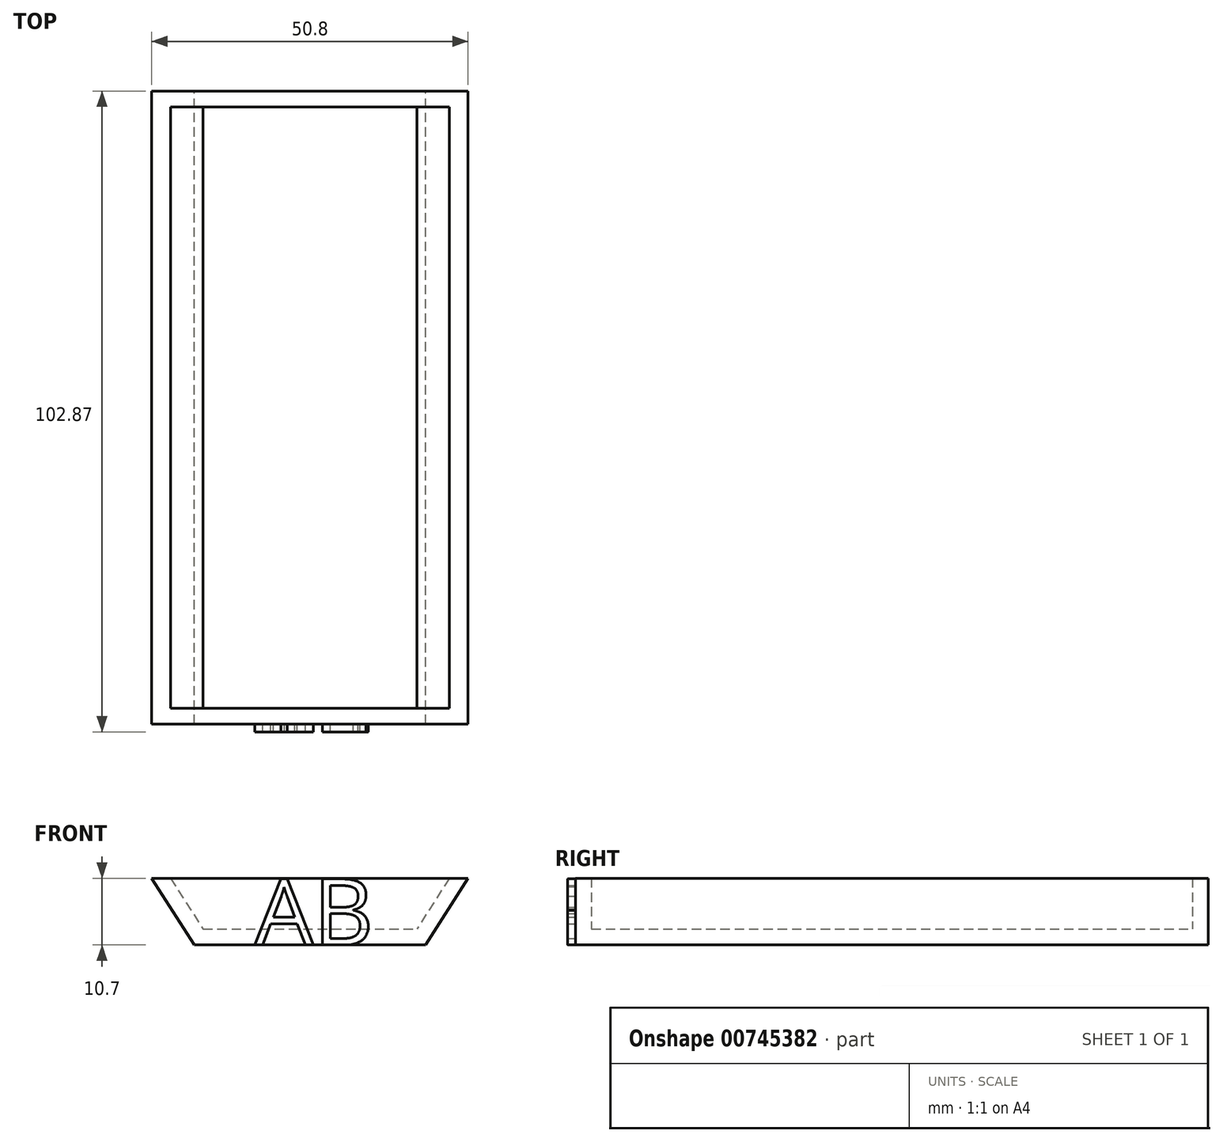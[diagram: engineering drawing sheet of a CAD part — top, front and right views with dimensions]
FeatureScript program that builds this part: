
annotation { "Feature Type Name" : "Feature", "Feature Type Description" : "" }
export const myFeature = defineFeature(function(context is Context, id is Id, definition is map)
    precondition{}
    {
        {
            var Q0;
            Q0=qCreatedBy(makeId("Front.planeOp"),FACE);
            var sketch = newSketch(context, id + "F0", { "sketchPlane" : qUnion([Q0])});
            skLineSegment(sketch, "E0", {"start": v(-50.8, 25.46) * mm, "end": v(0, 25.46) * mm});
            skLineSegment(sketch, "E1", {"start": v(-50.8, 25.46) * mm, "end": v(-43.95, 14.76) * mm});
            skLineSegment(sketch, "E2", {"start": v(0, 25.46) * mm, "end": v(-6.84, 14.76) * mm});
            skLineSegment(sketch, "E3", {"start": v(-43.95, 14.76) * mm, "end": v(-6.84, 14.76) * mm});
            skSolve(sketch);
        }
        {
            var Q0;
            Q0=makeQuery(id+"F0.imprint","IMPRINT",FACE,{"disambiguationData":[TD([[makeQuery(id+"F0.imprint","IMPRINT",EDGE,{"derivedFrom":sQuery(id+"F0.wireOp",EDGE,"E0")}),-1.0]])]});
            extrude(context, id + "F1", {"entities" : qUnion([Q0]), "depth" : 101.6 * mm, "offsetDistance" : 25.4 * mm});
        }
        {
            var Q0;
            Q0=makeQuery(id+"F1.opExtrude","SWEPT_FACE",FACE,{"disambiguationData":[OSD([sQuery(id+"F0.wireOp",EDGE,"E0")])]});
            shell(context, id + "F2", {"entities" : qUnion([Q0]), "thickness" : 2.54 * mm});
        }
        {
            var Q0;
            Q0=makeQuery(id+"F1.opExtrude","CAP_FACE",FACE,{"disambiguationData":[OSD([sQuery(id+"F0.wireOp",EDGE,"E0"),sQuery(id+"F0.wireOp",EDGE,"E1"),sQuery(id+"F0.wireOp",EDGE,"E2"),sQuery(id+"F0.wireOp",EDGE,"E3")])],"isStart":false});
            var sketch = newSketch(context, id + "F3", { "sketchPlane" : qUnion([Q0])});
            skText(sketch, "E4", { "text": "AB ", "fontName": "OpenSans-Regular.ttf"});
            const initialGuessF3  = {"E4": [-0.03425, 0.01476, 1, 0, 0.0107]};
            skSetInitialGuess(sketch, initialGuessF3);
            skSolve(sketch);
        }
        {
            var Q0;
            Q0 = qSketchRegion(id + "F3", true);
            extrude(context, id + "F4", {"entities" : qUnion([Q0]), "operationType" : NewBodyOperationType.ADD, "depth" : 1.27 * mm, "offsetDistance" : 25.4 * mm});
        }
    });
